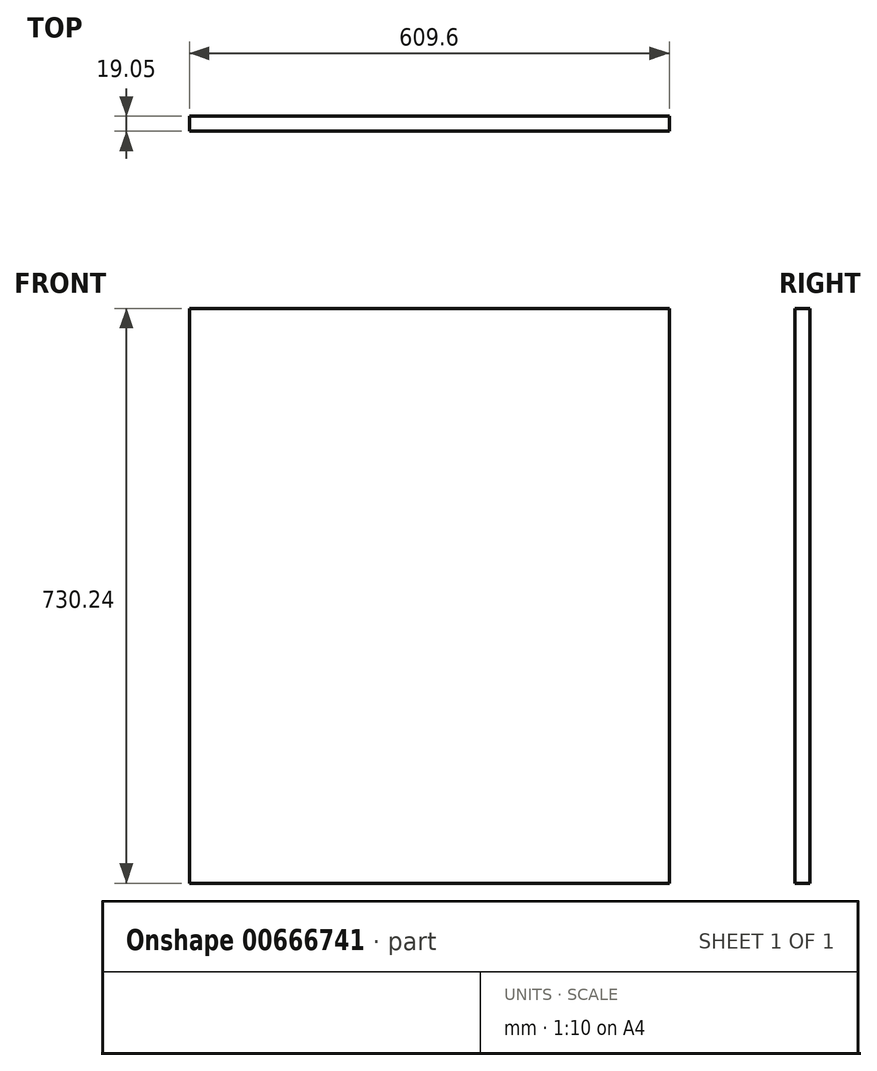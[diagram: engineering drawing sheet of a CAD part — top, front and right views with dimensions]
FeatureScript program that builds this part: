
annotation { "Feature Type Name" : "Feature", "Feature Type Description" : "" }
export const myFeature = defineFeature(function(context is Context, id is Id, definition is map)
    precondition{}
    {
        {
            var Q0;
            Q0=qCreatedBy(makeId("Front.planeOp"),FACE);
            var sketch = newSketch(context, id + "F0", { "sketchPlane" : qUnion([Q0])});
            skLineSegment(sketch, "E0.bottom", {"start": v(-304.8, 365.12) * mm, "end": v(304.8, 365.12) * mm});
            skLineSegment(sketch, "E0.top", {"start": v(-304.8, -365.13) * mm, "end": v(304.8, -365.13) * mm});
            skLineSegment(sketch, "E0.left", {"start": v(-304.8, 365.12) * mm, "end": v(-304.8, -365.13) * mm});
            skLineSegment(sketch, "E0.right", {"start": v(304.8, 365.12) * mm, "end": v(304.8, -365.13) * mm});
            skPoint(sketch, "E0.middle", {"position": v(0, 0) * mm});
            skSolve(sketch);
        }
        {
            var Q0;
            Q0=makeQuery(id+"F0.imprint","IMPRINT",FACE,{"disambiguationData":[TD([[makeQuery(id+"F0.imprint","IMPRINT",EDGE,{"derivedFrom":sQuery(id+"F0.wireOp",EDGE,"E0.bottom")}),-1.0]])]});
            extrude(context, id + "F1", {"entities" : qUnion([Q0]), "depth" : 19.05 * mm, "offsetDistance" : 25.4 * mm});
        }
    });
